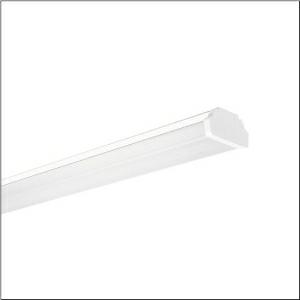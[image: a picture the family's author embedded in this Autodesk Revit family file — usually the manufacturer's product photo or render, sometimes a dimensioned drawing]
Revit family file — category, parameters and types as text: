
# Revit family: dus_31_gen_2_53bd812dv4d5d23sl3_8c21
name_source: partatom
category: Lighting Fixtures
units: mm (PartAtom-declared; Revit-internal decimal feet)

## family parameters
Cut with Voids When Loaded = No
Host = Face
Light Source = No
Part Type = Normal
Room Calculation Point = No
Round Connector Dimension = Use Diameter
Shared = No

## types (1)
- --- (1 x LED, 940 lm, 7.5 W, 4000K)
    Apparent Load = 8 VA
    CIE Flux Codes = 47 80 95 93 100
    Color Rendering = 80
    Color Temperature = 4000K
    Default Elevation = 1800 mm
    Description = DUS 31 Gen.2, luminaire insert, of sheet steel, coil coated, white, length: 1.535mm, width: 81mm, height: 90mm, 5x system unit, system units: 307mm, LED rated luminous flux: 13.680lm, light colour: 840, SDCM (Standard Deviation of Colour Matching)MacAdam ≤ 3 SDCM (initial), control gear: DALI 2, with plug, 6-pole, with phase selection (L1, L2), mains connection: 220..240V, AC, 50/60Hz, rated input power: 79W, for emergency light function, charging phase on L3 (wire number 3), through-wiring accessed according to module size, converter,control gear: single battery element, battery: LiFePO4, 9Ah, primary optical cover: cover, of PMMA, light emission: direct distribution, primary light characteristic: symmetric, protection rating (complete): IP20, protection rating (LED compartment): IP50, insulation class (complete): insulation class I (protective earthing), certification: CE, UKCA, impact resistance: IK03, permissible ambient temperature for indoor applications: +5..+35°C, standard: EN 60598-2-22, corresponds to IFS (International Featured Standards) requirements for safety and quality in the food industry, reducing of maximum allowable ambient temperature of 5°C with ceiling mounting, packaging unit: 1 piece
    Height = 95 mm
    Lamp = 1 x LED
    Lamp Light Flux = 940 lm
    Lamp Power = 7.5 W
    Lamp count = 1
    Length = 1535 mm
    Luminous efficacy = 125 lm/W
    Manufacturer = Siteco
    ModVariant = No
    Model = 53BD812DV4D5D23SL3
    Mounting Place = Ceiling
    Mounting Type = Pendant
    Number of Poles = 1
    OnlyDefault = Yes
    Power Factor = 1
    Product Name = DUS 31 Gen.2
    Product group = luminaire insert | ceiling pendant
    ProductGroupID = 901
    Protection Class = Protection class I
    Protection Degree = IP 20
    RLX_Detail_Level = 1
    RLX_Emergency_Light_Flux = 0 lm
    RLX_Emergency_Type = 0
    RLX_Emergency_Type_DB = No
    RlxData = <blob elided: 32605 chars, md5=3742cc4a>
    Socket = socket
    Standby Power = 0 W
    System Light Flux = 940 lm
    System Power = 8 W
    Type Comments = : emergency light operation: 3 h
    Type Image = l_1319596.jpg
    URL = http://relux.com
    VarID = @adj_037005
    Voltage = 0 V
    Weight = 0.00 kg
    Width = 81 mm

## geometry (parser evidence)
native form markers: Blend x4, Sweep x13
no freeform markers — native parametric forms only
